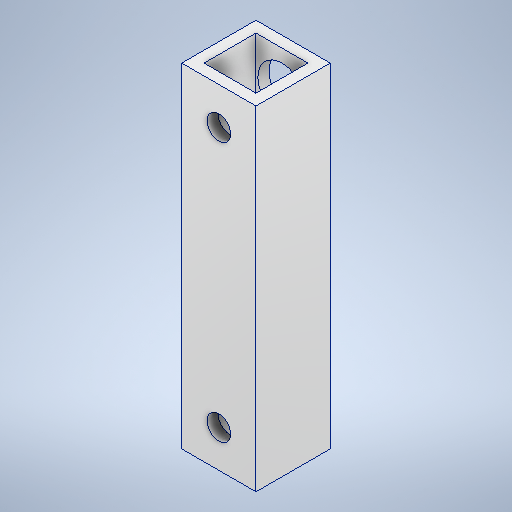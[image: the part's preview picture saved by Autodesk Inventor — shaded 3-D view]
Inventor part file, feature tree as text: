
AUTODESK INVENTOR PART (.ipt)
format: ipt  version: 2025 (Build 290162000, 162)  size: 295,424 bytes
history: native  units: mm
features: sketch x3, hole x2, other x1, extrude x1, mirror x1
ambient origin geometry x8: Origin, YZ Plane, XZ Plane, XY Plane, X Axis, Y Axis, Z Axis, Center Point
bodies: Body1 (feature_tree)
feature tree (8):
  other  "Těleso1"
  extrude  "Vysunutí1"  Depth=10.0mm
  hole  "Díra1"  [1 undecoded]
  hole  "Díra2"  [1 undecoded]
  mirror  "Zrcadlit1"
  sketch  "Náčrt1"
  sketch  "Náčrt2"
  sketch  "Náčrt3"
note: 2 required parameter values undecoded (feature->parameter linkage not recoverable at this tier; creation-order binding heuristic only, values carry confidence <= 0.55)
